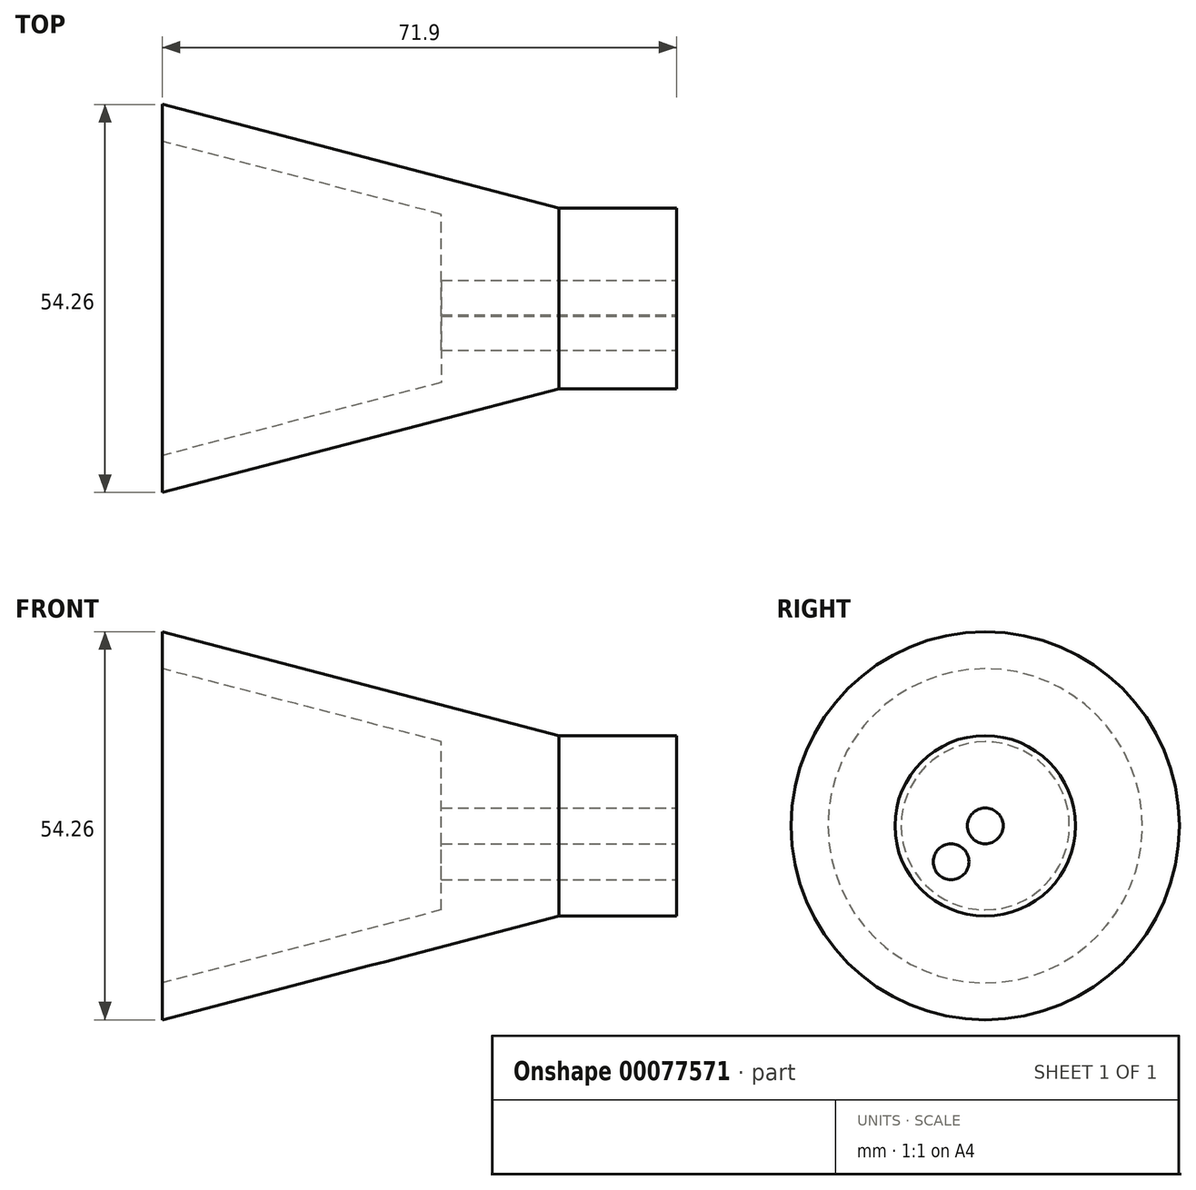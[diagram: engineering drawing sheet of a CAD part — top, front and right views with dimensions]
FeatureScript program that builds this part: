
annotation { "Feature Type Name" : "Feature", "Feature Type Description" : "" }
export const myFeature = defineFeature(function(context is Context, id is Id, definition is map)
    precondition{}
    {
        {
            var Q0;
            Q0=qCreatedBy(makeId("Front.planeOp"),FACE);
            var sketch = newSketch(context, id + "F0", { "sketchPlane" : qUnion([Q0])});
            skLineSegment(sketch, "E0", {"start": v(130, 0) * mm, "end": v(-115.1, 0) * mm, "construction": true});
            skLineSegment(sketch, "E1", {"start": v(0, -12.62) * mm, "end": v(-55.46, -27.13) * mm});
            skLineSegment(sketch, "E2", {"start": v(-55.46, -27.13) * mm, "end": v(-55.46, 0) * mm});
            skLineSegment(sketch, "E3", {"start": v(-55.46, 0) * mm, "end": v(0, 0) * mm});
            skLineSegment(sketch, "E4", {"start": v(0, 0) * mm, "end": v(0, -12.62) * mm});
            skSolve(sketch);
        }
        {
            var Q0;
            Q0=makeQuery(id+"F0.imprint","IMPRINT",FACE,{"disambiguationData":[TD([[makeQuery(id+"F0.imprint","IMPRINT",EDGE,{"derivedFrom":sQuery(id+"F0.wireOp",EDGE,"E1")}),-1.0]])]});
            var Q1;
            Q1=sQuery(id+"F0.wireOp",EDGE,"E0");
            revolve(context, id + "F1", {"entities" : qUnion([Q0]), "axis" : qUnion([Q1]), "revolveType" : RevolveType.FULL});
        }
        {
            var Q0;
            Q0=makeQuery(id+"F1.opRevolve","SWEPT_FACE",FACE,{"disambiguationData":[OSD([sQuery(id+"F0.wireOp",EDGE,"E2")])]});
            shell(context, id + "F2", {"entities" : qUnion([Q0]), "thickness" : 5 * mm});
        }
        {
            var Q0;
            Q0=makeQuery(id+"F1.opRevolve","SWEPT_FACE",FACE,{"disambiguationData":[OSD([sQuery(id+"F0.wireOp",EDGE,"E4")])]});
            var sketch = newSketch(context, id + "F3", { "sketchPlane" : qUnion([Q0])});
            skPoint(sketch, "E5", {"position": v(0, 0) * mm});
            skPoint(sketch, "E6", {"position": v(-4.78, -5.03) * mm});
            skSolve(sketch);
        }
        {
            var Q0;
            Q0=sQuery(id+"F3.wireOp",VERTEX,"E5");
            var Q1;
            Q1=sQuery(id+"F3.wireOp",VERTEX,"E6");
            var Q2;
            Q2=makeQuery(id+"F1.opRevolve","SWEPT_BODY",BODY,{"disambiguationData":[OSD([sQuery(id+"F0.wireOp",EDGE,"E1"),sQuery(id+"F0.wireOp",EDGE,"E2"),sQuery(id+"F0.wireOp",EDGE,"E3"),sQuery(id+"F0.wireOp",EDGE,"E4")])]});
            hole(context, id + "F4", {"style" : HoleStyle.SIMPLE, "endStyle" : HoleEndStyle.THROUGH, "holeDiameter" : 5 * mm, "locations" : qUnion([Q0, Q1]), "scope" : qUnion([Q2]), "isTappedThrough" : true});
        }
        {
            var Q0;
            Q0=makeQuery(id+"F1.opRevolve","SWEPT_FACE",FACE,{"disambiguationData":[OSD([sQuery(id+"F0.wireOp",EDGE,"E4")])]});
            extrude(context, id + "F5", {"entities" : qUnion([Q0]), "operationType" : NewBodyOperationType.ADD, "endBound" : BoundingType.SYMMETRIC, "depth" : 32.88 * mm});
        }
    });
